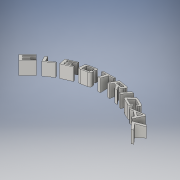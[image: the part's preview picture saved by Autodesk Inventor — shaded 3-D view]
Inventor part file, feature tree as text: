
AUTODESK INVENTOR PART (.ipt)
format: ipt  version: 2016 (Build 200138000, 138)  size: 532,480 bytes
history: native  units: in
note: dims shown in document units (in); Inventor stores cm internally (conversion verified against a paired STEP export)
features: sketch x3, extrude x2, projected_geometry x2, revolve x1
ambient origin geometry x8: Origin, YZ Plane, XZ Plane, XY Plane, X Axis, Y Axis, Z Axis, Center Point
bodies: Solid1 (feature_tree)
feature tree (8):
  revolve  "Revolution1"  [1 undecoded]
  extrude  "Extrusion1"  Depth=0.1in
  extrude  "Extrusion2"  Depth=0.275in
  sketch  "Sketch1"  dims[d0=0.8265in d1=0.175in]
  sketch  "Sketch2"  dims[d2=0.05in d3=0.1in]
  projected_geometry  "Projected Loop1"
  sketch  "Sketch3"  dims[d4=0.15in d5=0.275in d6=90.0deg d7=0.1in d18=0.05in d21=0.025in d22=0.125in d23=0.8in d24=0.025in d25=0.0125in d26=0.05in d27=0.025in d28=0.0125in d29=0.135in d30=0.135in d31=0.025in d32=0.025in d33=0.0125in d34=0.15in d35=0.05in d36=0.3in d37=0.025in d38=0.0125in d39=0.135in d40=0.3in d42=0.025in d43=0.135in d44=0.0451in d45=0.0451in d46=0.025in d47=0.0125in d48=0.05in d49=0.3in d50=0.025in d51=0.0125in d52=0.3in d53=0.135in d54=0.025in d55=0.135in d56=0.05in d57=0.025in d58=0.0125in d59=0.15in d60=0.135in d61=0.1in d62=0.075in d63=0.025in d64=0.025in d65=0.025in d66=0.8in d67=0.025in d68=0.0125in d69=0.1in d70=0.0in d71=0.075in d72=1.0in d73=0.0in]
  projected_geometry  "Projected Loop2"
note: 1 required parameter value undecoded (feature->parameter linkage not recoverable at this tier; creation-order binding heuristic only, values carry confidence <= 0.55)
